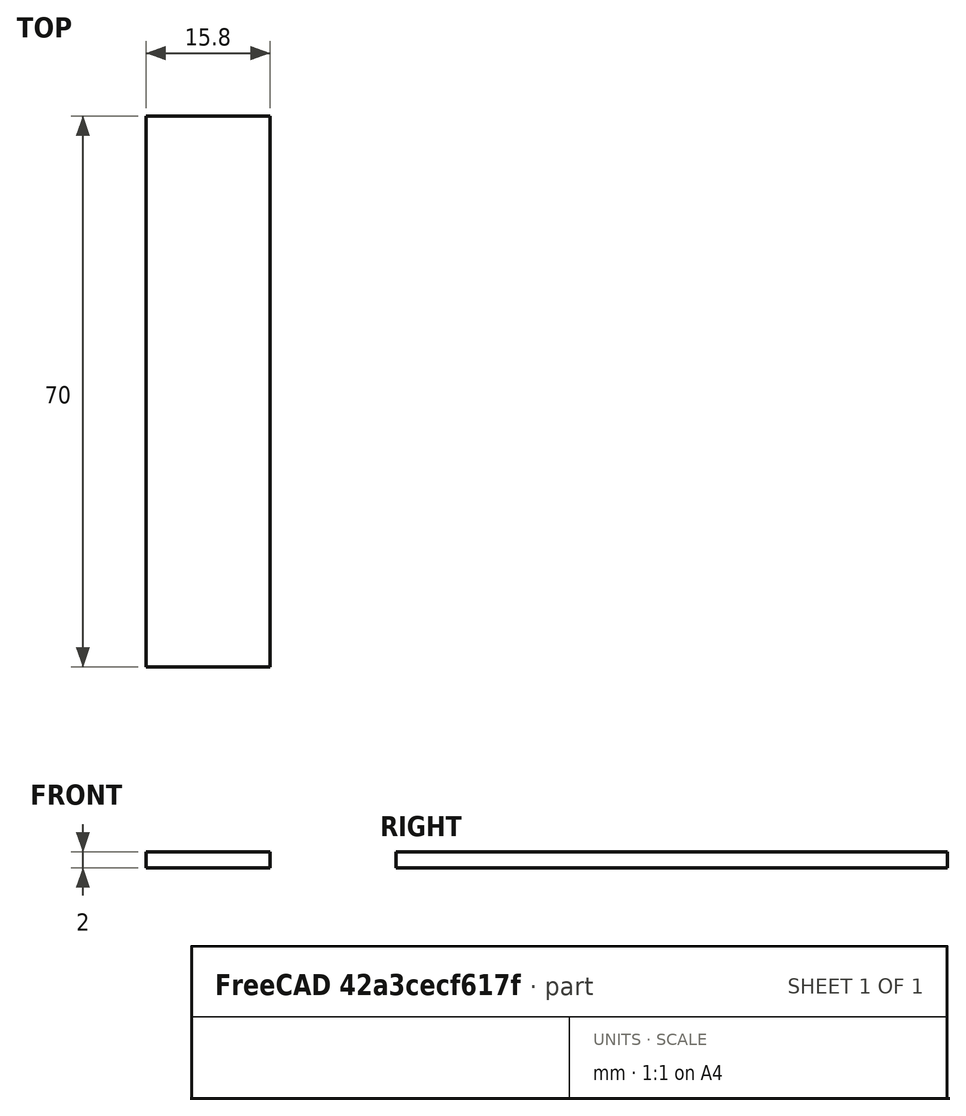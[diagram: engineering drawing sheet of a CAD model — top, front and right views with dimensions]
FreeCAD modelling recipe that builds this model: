
FCSTD DOCUMENT  (FreeCAD 0.19R24276 (Git))
Label: plat_16_70
License: All rights reserved
LicenseURL: http://en.wikipedia.org/wiki/All_rights_reserved
objects: Sketcher::SketchObject×1, PartDesign::Pad×1, PartDesign::Body×1
note: 4 computed .brp shape members not serialized (recipe doc carries the construction recipe); baked Part::Feature solids carry a one-line shape summary decoded from their .brp

FEATURE [Sketcher::SketchObject] Sketch
  FullyConstrained = true
  MapMode = 5
  Support = -> [XY_Plane]
  sketch-geometry (4):
    g0: LineSegment StartX=-7.9 StartY=35 StartZ=0 EndX=7.9 EndY=35 EndZ=0
    g1: LineSegment StartX=7.9 StartY=35 StartZ=0 EndX=7.9 EndY=-35 EndZ=0
    g2: LineSegment StartX=7.9 StartY=-35 StartZ=0 EndX=-7.9 EndY=-35 EndZ=0
    g3: LineSegment StartX=-7.9 StartY=-35 StartZ=0 EndX=-7.9 EndY=35 EndZ=0
  constraints (10):
    c: Coincident(g0,g1)
    c: Coincident(g1,g2)
    c: Coincident(g2,g3)
    c: Coincident(g3,g0)
    c: Horizontal(g2)
    c: Vertical(g1)
    c: DistanceX(g0,g0) = 15.8
    c: DistanceY(g1,g1) = 70
    c: Symmetric(g0,g0,g-2)
    c: Symmetric(g0,g2,g-1)
FEATURE [PartDesign::Pad] Pad  label="Pad_2mm"
  Direction = (1,1,1)
  Length = 2
  Length2 = 100
  Profile = -> Sketch
  Type = 0
FEATURE [PartDesign::Body] Body
  Group = -> [Sketch,Pad]
  Origin = -> Origin
  Tip = -> Pad
